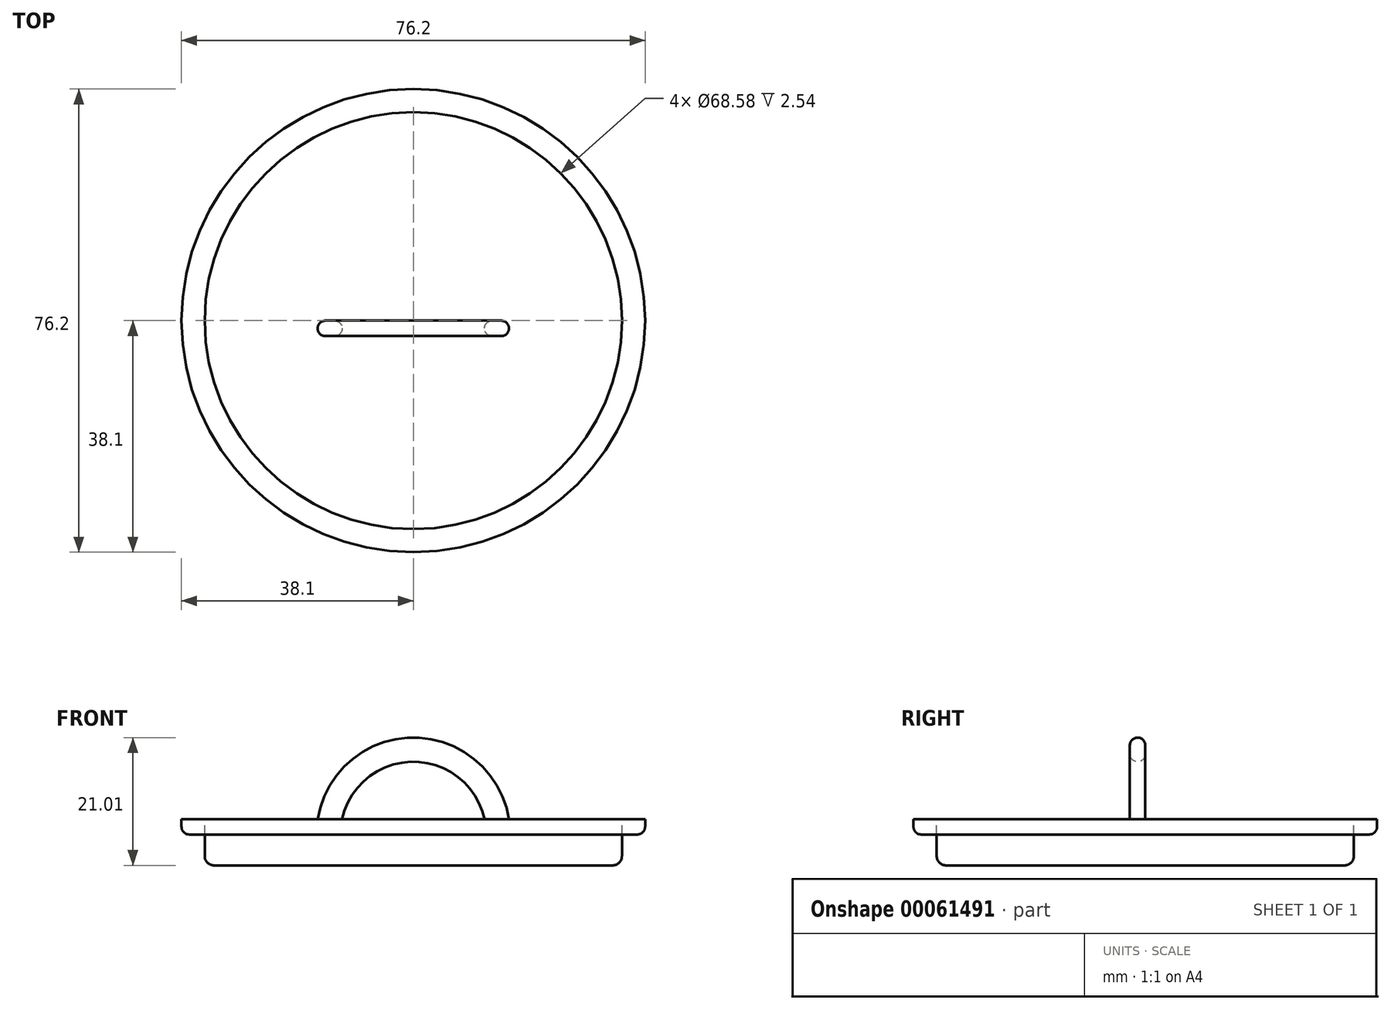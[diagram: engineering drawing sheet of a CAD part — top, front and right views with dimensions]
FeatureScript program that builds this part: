
annotation { "Feature Type Name" : "Feature", "Feature Type Description" : "" }
export const myFeature = defineFeature(function(context is Context, id is Id, definition is map)
    precondition{}
    {
        {
            var Q0;
            Q0=qCreatedBy(makeId("Top.planeOp"),FACE);
            var sketch = newSketch(context, id + "F0", { "sketchPlane" : qUnion([Q0])});
            skCircle(sketch, "E0", {"center": v(0, 0) * mm, "radius": 38.1 * mm});
            skCircle(sketch, "E1", {"center": v(0, 0) * mm, "radius": 34.3 * mm});
            skSolve(sketch);
        }
        {
            var Q0;
            Q0=makeQuery(id+"F0.imprint","IMPRINT",FACE,{"disambiguationData":[TD([[makeQuery(id+"F0.imprint","IMPRINT",EDGE,{"derivedFrom":sQuery(id+"F0.wireOp",EDGE,"E0")}),1.0]])]});
            extrude(context, id + "F1", {"entities" : qUnion([Q0]), "depth" : 2.54 * mm});
        }
        {
            var Q0;
            Q0=makeQuery(id+"F1.opExtrude","CAP_EDGE",EDGE,{"disambiguationData":[OSD([sQuery(id+"F0.wireOp",EDGE,"E0")])],"isStart":true});
            fillet(context, id + "F2", {"entities" : qUnion([Q0]), "radius" : 1.27 * mm, "tangentPropagation" : true, "allowEdgeOverflow" : false});
        }
        {
            var Q0;
            Q0=qCreatedBy(makeId("Front.planeOp"),FACE);
            var sketch = newSketch(context, id + "F3", { "sketchPlane" : qUnion([Q0])});
            skCircle(sketch, "E2", {"center": v(0, 0) * mm, "radius": 15.93 * mm});
            skCircle(sketch, "E3", {"center": v(0, 0) * mm, "radius": 11.97 * mm});
            skSolve(sketch);
        }
        {
            var Q0;
            Q0=makeQuery(id+"F3.imprint","IMPRINT",FACE,{"disambiguationData":[TD([[makeQuery(id+"F3.imprint","IMPRINT",EDGE,{"derivedFrom":sQuery(id+"F3.wireOp",EDGE,"E2")}),1.0]])]});
            extrude(context, id + "F4", {"entities" : qUnion([Q0]), "operationType" : NewBodyOperationType.ADD, "depth" : 2.54 * mm});
        }
        {
            var Q0;
            {var subQ0=sQuery(id+"F3.wireOp",EDGE,"E2");Q0=makeQuery(id+"F4.boolean.opBoolean","SPLIT",EDGE,{"disambiguationData":[TD([makeQuery(id+"F1.opExtrude","CAP_FACE",FACE,{"disambiguationData":[OSD([sQuery(id+"F0.wireOp",EDGE,"E0")])],"isStart":false})])],"derivedFrom":makeQuery(id+"F4.opExtrude","CAP_EDGE",EDGE,{"disambiguationData":[OSD([subQ0])],"isStart":false})});}
            var Q1;
            {var subQ0=sQuery(id+"F3.wireOp",EDGE,"E3");Q1=makeQuery(id+"F4.boolean.opBoolean","SPLIT",EDGE,{"disambiguationData":[TD([makeQuery(id+"F1.opExtrude","CAP_FACE",FACE,{"disambiguationData":[OSD([sQuery(id+"F0.wireOp",EDGE,"E0")])],"isStart":false})])],"derivedFrom":makeQuery(id+"F4.opExtrude","CAP_EDGE",EDGE,{"disambiguationData":[OSD([subQ0])],"isStart":true})});}
            var Q2;
            {var subQ0=sQuery(id+"F3.wireOp",EDGE,"E2");Q2=makeQuery(id+"F4.boolean.opBoolean","SPLIT",EDGE,{"disambiguationData":[TD([makeQuery(id+"F1.opExtrude","CAP_FACE",FACE,{"disambiguationData":[OSD([sQuery(id+"F0.wireOp",EDGE,"E0")])],"isStart":false})])],"derivedFrom":makeQuery(id+"F4.opExtrude","CAP_EDGE",EDGE,{"disambiguationData":[OSD([subQ0])],"isStart":true})});}
            var Q3;
            {var subQ0=sQuery(id+"F3.wireOp",EDGE,"E3");Q3=makeQuery(id+"F4.boolean.opBoolean","SPLIT",EDGE,{"disambiguationData":[TD([makeQuery(id+"F1.opExtrude","CAP_FACE",FACE,{"disambiguationData":[OSD([sQuery(id+"F0.wireOp",EDGE,"E0")])],"isStart":false})])],"derivedFrom":makeQuery(id+"F4.opExtrude","CAP_EDGE",EDGE,{"disambiguationData":[OSD([subQ0])],"isStart":false})});}
            fillet(context, id + "F5", {"entities" : qUnion([Q0, Q1, Q2, Q3]), "radius" : 1.27 * mm, "allowEdgeOverflow" : false});
        }
        {
            var Q0;
            Q0=makeQuery(id+"F0.imprint","IMPRINT",FACE,{"disambiguationData":[TD([[makeQuery(id+"F0.imprint","IMPRINT",EDGE,{"derivedFrom":sQuery(id+"F0.wireOp",EDGE,"E1")}),1.0]])]});
            extrude(context, id + "F6", {"entities" : qUnion([Q0]), "oppositeDirection" : true, "depth" : 5.08 * mm});
        }
        {
            var Q0;
            Q0=makeQuery(id+"F0.imprint","IMPRINT",FACE,{"disambiguationData":[TD([[makeQuery(id+"F0.imprint","IMPRINT",EDGE,{"derivedFrom":sQuery(id+"F0.wireOp",EDGE,"E1")}),1.0]])]});
            extrude(context, id + "F7", {"entities" : qUnion([Q0]), "depth" : 2.54 * mm});
        }
        {
            var Q0;
            Q0=makeQuery(id+"F6.opExtrude","CAP_EDGE",EDGE,{"disambiguationData":[OSD([sQuery(id+"F0.wireOp",EDGE,"E1")])],"isStart":false});
            fillet(context, id + "F8", {"entities" : qUnion([Q0]), "radius" : 1.52 * mm, "tangentPropagation" : true, "allowEdgeOverflow" : false});
        }
        {
            var Q0;
            Q0=makeQuery(id+"F6.opExtrude","CAP_FACE",FACE,{"disambiguationData":[OSD([sQuery(id+"F0.wireOp",EDGE,"E1")])],"isStart":false});
            var sketch = newSketch(context, id + "F9", { "sketchPlane" : qUnion([Q0])});
            skLineSegment(sketch, "E4.bottom", {"start": v(-16, 5.67) * mm, "end": v(16.18, 5.67) * mm});
            skLineSegment(sketch, "E4.top", {"start": v(-16, -3.21) * mm, "end": v(16.18, -3.21) * mm});
            skLineSegment(sketch, "E4.left", {"start": v(-16, 5.67) * mm, "end": v(-16, -3.21) * mm});
            skLineSegment(sketch, "E4.right", {"start": v(16.18, 5.67) * mm, "end": v(16.18, -3.21) * mm});
            skSolve(sketch);
        }
        {
            var Q0;
            Q0=makeQuery(id+"F9.imprint","IMPRINT",FACE,{"disambiguationData":[TD([[makeQuery(id+"F9.imprint","IMPRINT",EDGE,{"derivedFrom":sQuery(id+"F9.wireOp",EDGE,"E4.bottom")}),-1.0]])]});
            extrude(context, id + "F10", {"entities" : qUnion([Q0]), "operationType" : NewBodyOperationType.REMOVE, "depth" : 17.27 * mm});
        }
    });
